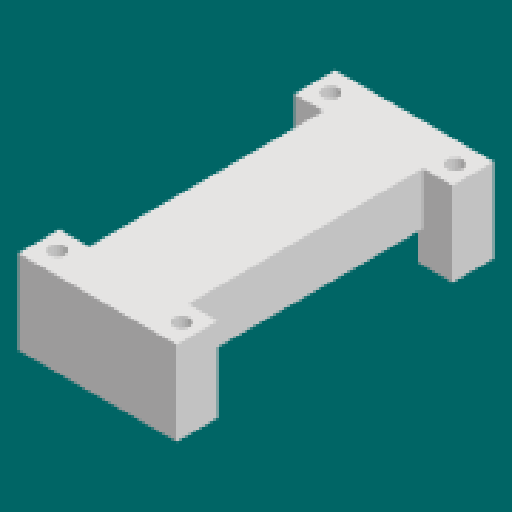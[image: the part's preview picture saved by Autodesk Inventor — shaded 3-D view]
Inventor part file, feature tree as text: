
AUTODESK INVENTOR PART (.ipt)
format: ipt  version: 2025.2 (Build 292293000, 293)  size: 207,360 bytes
history: native  units: mm
features: extrude x4, sketch x4
ambient origin geometry x8: Origin, YZ Plane, XZ Plane, XY Plane, X Axis, Y Axis, Z Axis, Center Point
bodies: Solid1 (feature_tree)
feature tree (8):
  extrude  "Extrusion1"  Depth=200.0mm
  extrude  "Extrusion2"  Depth=194.0mm
  extrude  "Extrusion3"  Depth=10.0mm
  extrude  "Extrusion4"  Depth=20.0mm
  sketch  "Sketch1"  dims[d0=100.0mm d1=200.0mm]
  sketch  "Sketch2"  dims[d2=94.0mm d3=194.0mm]
  sketch  "Sketch3"  dims[d4=23.0mm d6=10.0mm]
  sketch  "Sketch4"  dims[d7=7.833333mm d8=7.833333mm d9=3.0mm d10=0.0mm d11=3.0mm d12=3.0mm d13=3.0mm d14=3.0mm d15=3.0mm d16=30.0mm d17=0.0mm d18=20.0mm d19=0.0mm d21=0.0mm d22=0.0mm]
